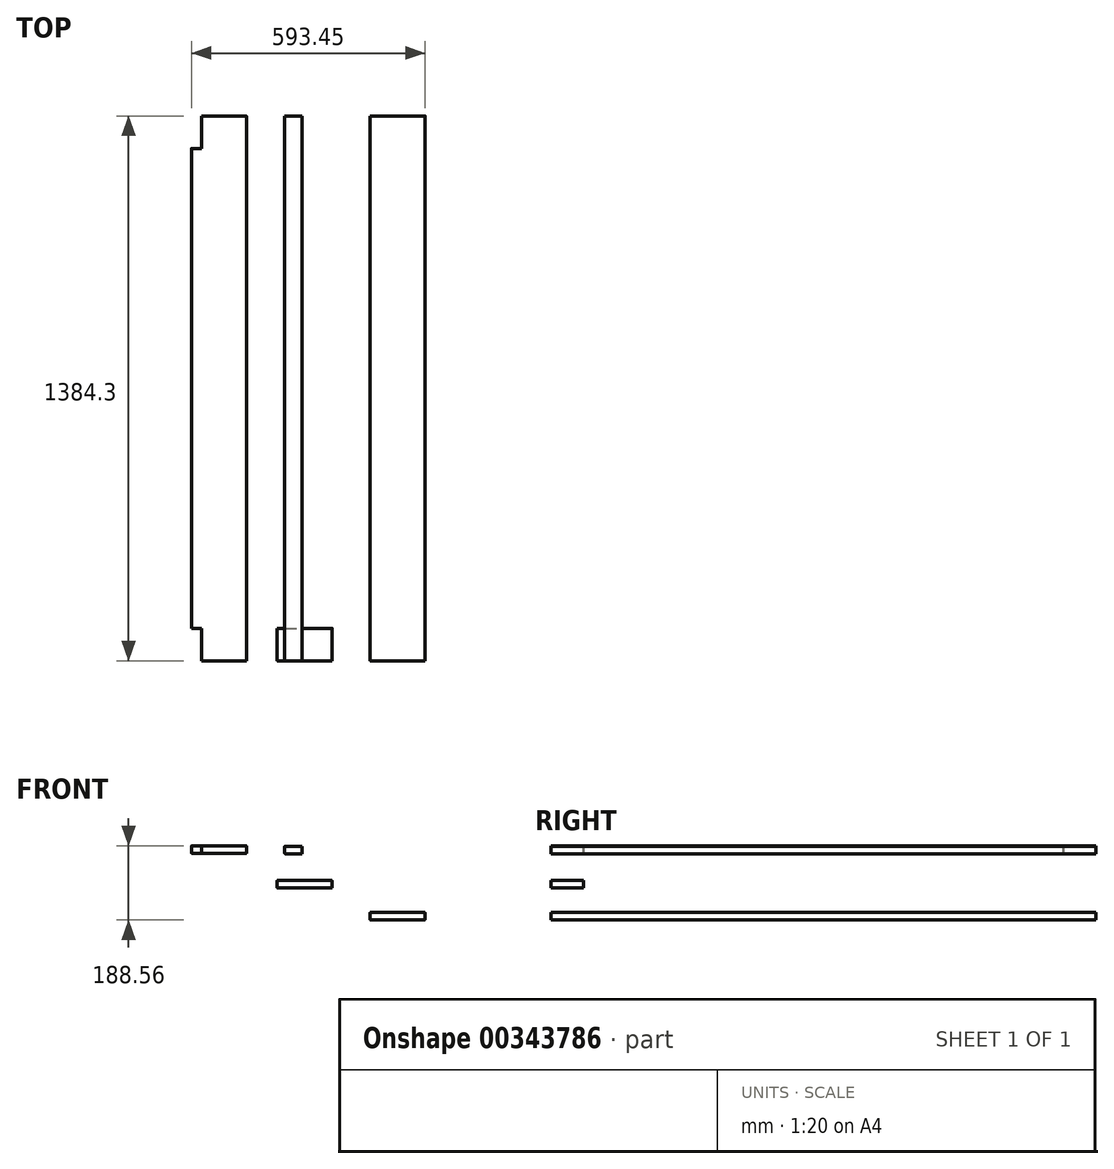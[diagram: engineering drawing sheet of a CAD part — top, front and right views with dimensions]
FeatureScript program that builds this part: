
annotation { "Feature Type Name" : "Feature", "Feature Type Description" : "" }
export const myFeature = defineFeature(function(context is Context, id is Id, definition is map)
    precondition{}
    {
        {
            var Q0;
            Q0=qCreatedBy(makeId("Front.planeOp"),FACE);
            var sketch = newSketch(context, id + "F0", { "sketchPlane" : qUnion([Q0])});
            skLineSegment(sketch, "E0.bottom", {"start": v(-72.33, 22.93) * mm, "end": v(66.1, 22.93) * mm});
            skLineSegment(sketch, "E0.top", {"start": v(-72.33, 3.88) * mm, "end": v(66.1, 3.88) * mm});
            skLineSegment(sketch, "E0.left", {"start": v(-72.96, 22.3) * mm, "end": v(-72.96, 4.51) * mm});
            skLineSegment(sketch, "E0.right", {"start": v(66.74, 22.3) * mm, "end": v(66.74, 4.51) * mm});
            skPoint(sketch, "E1.visualSharp", {"position": v(-72.96, 22.93) * mm});
            skArc(sketch, "E1.filletArc", {"start": v(-72.33, 22.93) * mm, "mid": v(-72.78, 22.74) * mm, "end": v(-72.96, 22.3) * mm});
            skPoint(sketch, "E2.visualSharp", {"position": v(66.74, 22.93) * mm});
            skArc(sketch, "E2.filletArc", {"start": v(66.74, 22.3) * mm, "mid": v(66.55, 22.74) * mm, "end": v(66.1, 22.93) * mm});
            skPoint(sketch, "E3.visualSharp", {"position": v(66.74, 3.88) * mm});
            skArc(sketch, "E3.filletArc", {"start": v(66.1, 3.88) * mm, "mid": v(66.55, 4.07) * mm, "end": v(66.74, 4.51) * mm});
            skPoint(sketch, "E4.visualSharp", {"position": v(-72.96, 3.88) * mm});
            skArc(sketch, "E4.filletArc", {"start": v(-72.96, 4.51) * mm, "mid": v(-72.78, 4.07) * mm, "end": v(-72.33, 3.88) * mm});
            skSolve(sketch);
        }
        {
            var Q0;
            Q0=makeQuery(id+"F0.imprint","IMPRINT",FACE,{"disambiguationData":[TD([[makeQuery(id+"F0.imprint","IMPRINT",EDGE,{"derivedFrom":sQuery(id+"F0.wireOp",EDGE,"E0.bottom")}),-1.0]])]});
            extrude(context, id + "F1", {"entities" : qUnion([Q0]), "oppositeDirection" : true, "depth" : 1384.3 * mm});
        }
        {
            var Q0;
            Q0=qCreatedBy(makeId("Front.planeOp"),FACE);
            var sketch = newSketch(context, id + "F2", { "sketchPlane" : qUnion([Q0])});
            skLineSegment(sketch, "E5.bottom", {"start": v(-308.63, 104.08) * mm, "end": v(-170.2, 104.08) * mm});
            skLineSegment(sketch, "E5.top", {"start": v(-308.63, 85.03) * mm, "end": v(-170.2, 85.03) * mm});
            skLineSegment(sketch, "E5.left", {"start": v(-309.26, 103.44) * mm, "end": v(-309.26, 85.66) * mm});
            skLineSegment(sketch, "E5.right", {"start": v(-169.56, 103.44) * mm, "end": v(-169.56, 85.66) * mm});
            skPoint(sketch, "E6.visualSharp", {"position": v(-309.26, 104.08) * mm});
            skArc(sketch, "E6.filletArc", {"start": v(-308.63, 104.08) * mm, "mid": v(-309.07, 103.9) * mm, "end": v(-309.26, 103.44) * mm});
            skPoint(sketch, "E7.visualSharp", {"position": v(-169.56, 104.08) * mm});
            skArc(sketch, "E7.filletArc", {"start": v(-169.56, 103.44) * mm, "mid": v(-169.75, 103.9) * mm, "end": v(-170.2, 104.08) * mm});
            skPoint(sketch, "E8.visualSharp", {"position": v(-169.56, 85.03) * mm});
            skArc(sketch, "E8.filletArc", {"start": v(-170.2, 85.03) * mm, "mid": v(-169.75, 85.21) * mm, "end": v(-169.56, 85.66) * mm});
            skPoint(sketch, "E9.visualSharp", {"position": v(-309.26, 85.03) * mm});
            skArc(sketch, "E9.filletArc", {"start": v(-309.26, 85.66) * mm, "mid": v(-309.07, 85.21) * mm, "end": v(-308.63, 85.03) * mm});
            skSolve(sketch);
        }
        {
            var Q0;
            Q0=makeQuery(id+"F2.imprint","IMPRINT",FACE,{"disambiguationData":[TD([[makeQuery(id+"F2.imprint","IMPRINT",EDGE,{"derivedFrom":sQuery(id+"F2.wireOp",EDGE,"E5.bottom")}),-1.0]])]});
            extrude(context, id + "F3", {"entities" : qUnion([Q0]), "oppositeDirection" : true, "depth" : 82.55 * mm});
        }
        {
            var Q0;
            Q0=qCreatedBy(makeId("Front.planeOp"),FACE);
            var sketch = newSketch(context, id + "F4", { "sketchPlane" : qUnion([Q0])});
            skLineSegment(sketch, "E10.bottom", {"start": v(-526.08, 192.44) * mm, "end": v(-387.65, 192.44) * mm});
            skLineSegment(sketch, "E10.top", {"start": v(-526.08, 173.4) * mm, "end": v(-387.65, 173.4) * mm});
            skLineSegment(sketch, "E10.left", {"start": v(-526.71, 191.8) * mm, "end": v(-526.71, 174.03) * mm});
            skLineSegment(sketch, "E10.right", {"start": v(-387.01, 191.8) * mm, "end": v(-387.01, 174.03) * mm});
            skPoint(sketch, "E11.visualSharp", {"position": v(-526.71, 192.44) * mm});
            skArc(sketch, "E11.filletArc", {"start": v(-526.08, 192.44) * mm, "mid": v(-526.53, 192.26) * mm, "end": v(-526.71, 191.8) * mm});
            skPoint(sketch, "E12.visualSharp", {"position": v(-387.01, 192.44) * mm});
            skArc(sketch, "E12.filletArc", {"start": v(-387.01, 191.8) * mm, "mid": v(-387.2, 192.26) * mm, "end": v(-387.65, 192.44) * mm});
            skPoint(sketch, "E13.visualSharp", {"position": v(-387.01, 173.4) * mm});
            skArc(sketch, "E13.filletArc", {"start": v(-387.65, 173.4) * mm, "mid": v(-387.2, 173.58) * mm, "end": v(-387.01, 174.03) * mm});
            skPoint(sketch, "E14.visualSharp", {"position": v(-526.71, 173.4) * mm});
            skArc(sketch, "E14.filletArc", {"start": v(-526.71, 174.03) * mm, "mid": v(-526.53, 173.58) * mm, "end": v(-526.08, 173.4) * mm});
            skSolve(sketch);
        }
        {
            var Q0;
            Q0=makeQuery(id+"F4.imprint","IMPRINT",FACE,{"disambiguationData":[TD([[makeQuery(id+"F4.imprint","IMPRINT",EDGE,{"derivedFrom":sQuery(id+"F4.wireOp",EDGE,"E10.bottom")}),-1.0]])]});
            extrude(context, id + "F5", {"entities" : qUnion([Q0]), "oppositeDirection" : true, "depth" : 1384.3 * mm});
        }
        {
            var Q0;
            Q0=makeQuery(id+"F5.opExtrude","SWEPT_FACE",FACE,{"disambiguationData":[OSD([sQuery(id+"F4.wireOp",EDGE,"E10.bottom")])]});
            var sketch = newSketch(context, id + "F6", { "sketchPlane" : qUnion([Q0])});
            skLineSegment(sketch, "E15.bottom", {"start": v(-526.72, 1384.3) * mm, "end": v(-501.32, 1384.3) * mm});
            skLineSegment(sketch, "E15.top", {"start": v(-526.72, 1301.75) * mm, "end": v(-501.32, 1301.75) * mm});
            skLineSegment(sketch, "E15.left", {"start": v(-526.72, 1384.3) * mm, "end": v(-526.72, 1301.75) * mm});
            skLineSegment(sketch, "E15.right", {"start": v(-501.32, 1384.3) * mm, "end": v(-501.32, 1301.75) * mm});
            skLineSegment(sketch, "E16.bottom", {"start": v(-526.7, 0) * mm, "end": v(-501.3, 0) * mm});
            skLineSegment(sketch, "E16.top", {"start": v(-526.7, 82.55) * mm, "end": v(-501.3, 82.55) * mm});
            skLineSegment(sketch, "E16.left", {"start": v(-526.7, 0) * mm, "end": v(-526.7, 82.55) * mm});
            skLineSegment(sketch, "E16.right", {"start": v(-501.3, 0) * mm, "end": v(-501.3, 82.55) * mm});
            skSolve(sketch);
        }
        {
            var Q0;
            {var subQ4=sQuery(id+"F6.wireOp",EDGE,"E16.right");Q0=makeQuery(id+"F6.imprint","IMPRINT",FACE,{"disambiguationData":[TD([[makeQuery(id+"F6.imprint","IMPRINT",EDGE,{"derivedFrom":subQ4}),1.0]])]});}
            var Q1;
            {var subQ4=sQuery(id+"F6.wireOp",EDGE,"E15.right");Q1=makeQuery(id+"F6.imprint","IMPRINT",FACE,{"disambiguationData":[TD([[makeQuery(id+"F6.imprint","IMPRINT",EDGE,{"derivedFrom":subQ4}),-1.0]])]});}
            extrude(context, id + "F7", {"entities" : qUnion([Q0, Q1]), "operationType" : NewBodyOperationType.REMOVE, "endBound" : BoundingType.THROUGH_ALL, "oppositeDirection" : true, "depth" : 25.4 * mm});
        }
        {
            var Q0;
            {var subQ0=sQuery(id+"F4.wireOp",EDGE,"E11.filletArc");var subQ1=sQuery(id+"F4.wireOp",EDGE,"E10.bottom");var subQ2=makeQuery(id+"F5.opExtrude","SWEPT_EDGE",EDGE,{"disambiguationData":[OSD([subQ1,subQ0])]});Q0=makeQuery(id+"F7.boolean.opBoolean","COPY",FACE,{"derivedFrom":makeQuery(id+"F7.opExtrude","SWEPT_FACE",FACE,{"disambiguationData":[OSD([subQ1,subQ0]),TDD([makeQuery(id+"F6.imprint","IMPRINT",EDGE,{"disambiguationData":[TD([[makeQuery(id+"F6.imprint","INTERSECT",VERTEX,{"derivedFrom":[subQ2,sQuery(id+"F6.wireOp",EDGE,"E16.bottom")]}),1.0]])],"derivedFrom":subQ2})])]})});}
            var Q1;
            {var subQ0=sQuery(id+"F4.wireOp",EDGE,"E11.filletArc");var subQ1=sQuery(id+"F4.wireOp",EDGE,"E10.bottom");var subQ2=makeQuery(id+"F5.opExtrude","SWEPT_EDGE",EDGE,{"disambiguationData":[OSD([subQ1,subQ0])]});Q1=makeQuery(id+"F7.boolean.opBoolean","COPY",FACE,{"derivedFrom":makeQuery(id+"F7.opExtrude","SWEPT_FACE",FACE,{"disambiguationData":[OSD([subQ1,subQ0]),TDD([makeQuery(id+"F6.imprint","IMPRINT",EDGE,{"disambiguationData":[TD([[makeQuery(id+"F6.imprint","INTERSECT",VERTEX,{"derivedFrom":[subQ2,sQuery(id+"F6.wireOp",EDGE,"E15.bottom")]}),-1.0]])],"derivedFrom":subQ2})])]})});}
            extrude(context, id + "F8", {"entities" : qUnion([Q0, Q1]), "operationType" : NewBodyOperationType.REMOVE, "oppositeDirection" : true, "depth" : 25.4 * mm});
        }
        {
            var Q0;
            Q0=qCreatedBy(makeId("Front.planeOp"),FACE);
            var sketch = newSketch(context, id + "F9", { "sketchPlane" : qUnion([Q0])});
            skLineSegment(sketch, "E17.bottom", {"start": v(-289.03, 191.33) * mm, "end": v(-245.85, 191.33) * mm});
            skLineSegment(sketch, "E17.top", {"start": v(-289.03, 172.28) * mm, "end": v(-245.85, 172.28) * mm});
            skLineSegment(sketch, "E17.left", {"start": v(-289.67, 190.7) * mm, "end": v(-289.67, 172.92) * mm});
            skLineSegment(sketch, "E17.right", {"start": v(-245.22, 190.7) * mm, "end": v(-245.22, 172.92) * mm});
            skPoint(sketch, "E18.visualSharp", {"position": v(-289.67, 191.33) * mm});
            skArc(sketch, "E18.filletArc", {"start": v(-289.03, 191.33) * mm, "mid": v(-289.48, 191.14) * mm, "end": v(-289.67, 190.7) * mm});
            skPoint(sketch, "E19.visualSharp", {"position": v(-245.22, 191.33) * mm});
            skPoint(sketch, "E20.visualSharp", {"position": v(-245.22, 172.28) * mm});
            skPoint(sketch, "E21.visualSharp", {"position": v(-289.67, 172.28) * mm});
            skArc(sketch, "E21.filletArc", {"start": v(-289.67, 172.92) * mm, "mid": v(-289.48, 172.47) * mm, "end": v(-289.03, 172.28) * mm});
            skLineSegment(sketch, "E22.bottom", {"start": v(-245.85, 191.33) * mm, "end": v(-245.22, 191.33) * mm});
            skLineSegment(sketch, "E22.right", {"start": v(-245.22, 191.33) * mm, "end": v(-245.22, 190.7) * mm});
            skLineSegment(sketch, "E23.bottom", {"start": v(-245.85, 172.28) * mm, "end": v(-245.22, 172.28) * mm});
            skLineSegment(sketch, "E23.right", {"start": v(-245.22, 172.28) * mm, "end": v(-245.22, 172.92) * mm});
            skSolve(sketch);
        }
        {
            var Q0;
            Q0 = qSketchRegion(id + "F9", true);
            extrude(context, id + "F10", {"entities" : qUnion([Q0]), "oppositeDirection" : true, "depth" : 1384.3 * mm});
        }
    });
